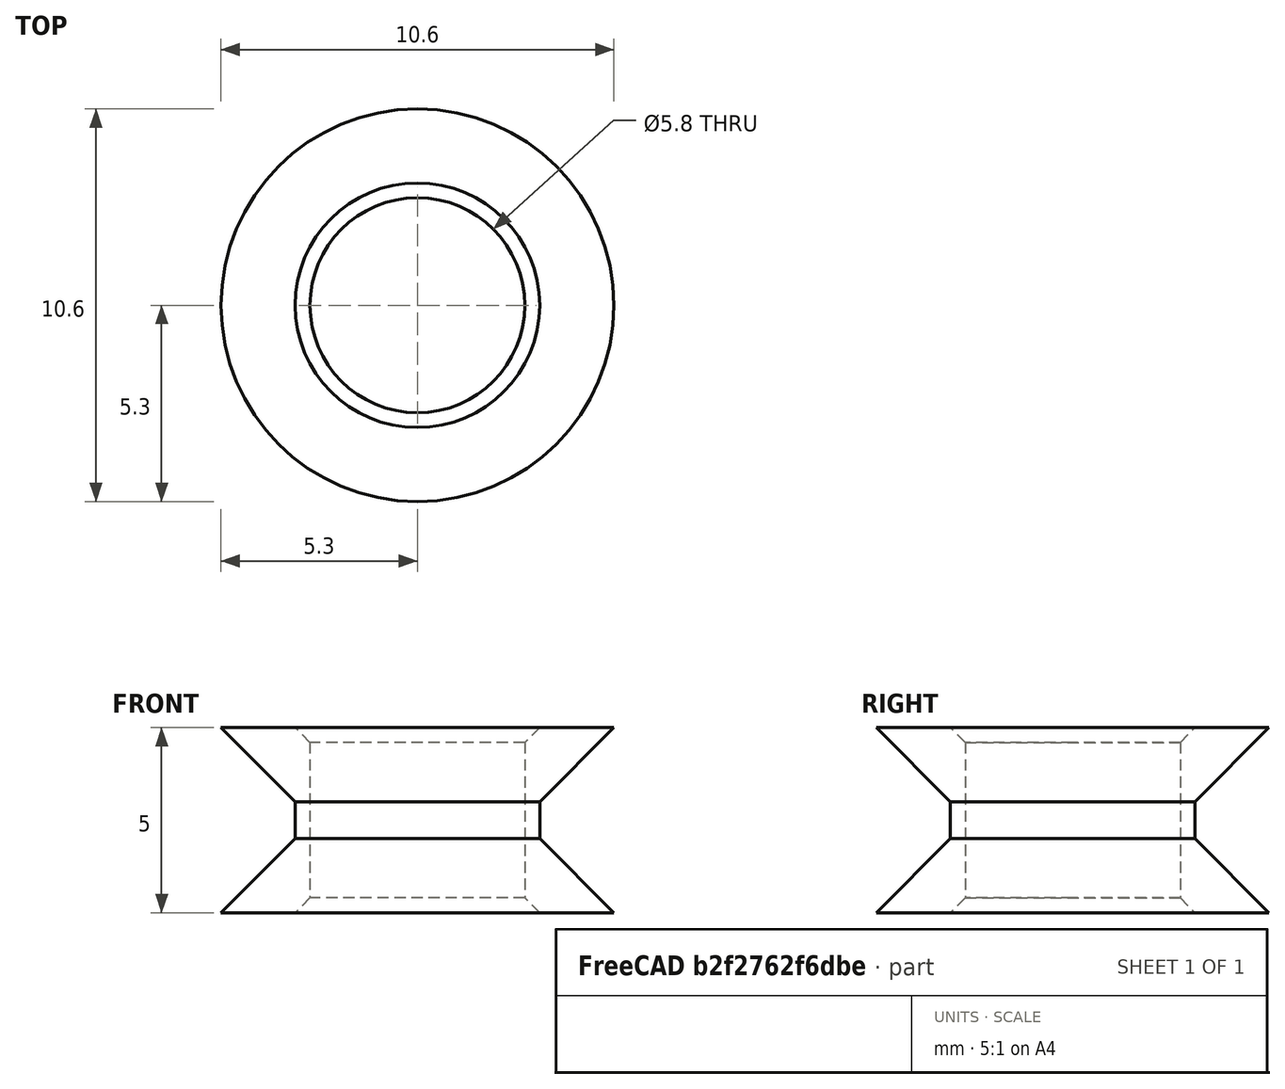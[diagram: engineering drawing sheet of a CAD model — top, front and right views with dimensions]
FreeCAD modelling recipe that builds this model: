
FCSTD DOCUMENT  (FreeCAD 0.18R4 (GitTag))
Label: Ring
License: All rights reserved
LicenseURL: http://en.wikipedia.org/wiki/All_rights_reserved
objects: Sketcher::SketchObject×1, PartDesign::Revolution×1, PartDesign::Chamfer×1, PartDesign::Body×1, Mesh::Feature×1
note: 5 computed .brp shape members not serialized (recipe doc carries the construction recipe); baked Part::Feature solids carry a one-line shape summary decoded from their .brp

FEATURE [Sketcher::SketchObject] Sketch
  MapMode = 5
  Placement = pos=(0,0,0) rot=(1,0,0;1.5708rad)
  Support = -> [XZ_Plane001]
  sketch-geometry (6):
    g0: LineSegment StartX=2.9 StartY=-2.5 StartZ=0 EndX=5.3 EndY=-2.5 EndZ=0
    g1: LineSegment StartX=5.3 StartY=-2.5 StartZ=0 EndX=3.3 EndY=-0.5 EndZ=0
    g2: LineSegment StartX=3.3 StartY=-0.5 StartZ=0 EndX=3.3 EndY=0.5 EndZ=0
    g3: LineSegment StartX=3.3 StartY=0.5 StartZ=0 EndX=5.3 EndY=2.5 EndZ=0
    g4: LineSegment StartX=5.3 StartY=2.5 StartZ=0 EndX=2.9 EndY=2.5 EndZ=0
    g5: LineSegment StartX=2.9 StartY=2.5 StartZ=0 EndX=2.9 EndY=-2.5 EndZ=0
  constraints (16):
    c: Horizontal(g0)
    c: Coincident(g0,g1)
    c: Coincident(g1,g2)
    c: Coincident(g2,g3)
    c: Coincident(g3,g4)
    c: Horizontal(g4)
    c: Coincident(g4,g5)
    c: Coincident(g5,g0)
    c: Vertical(g5)
    c: Symmetric(g2,g1,g-1)
    c: Symmetric(g3,g0,g-1)
    c: DistanceY(g5,g5) = 5
    c: DistanceY(g2,g4) = 2
    c: DistanceX(g2,g3) = 2
    c: DistanceX(g-1,g0) = 2.9
    c: DistanceX(g0,g1) = 0.4
FEATURE [PartDesign::Revolution] Revolution
  Angle = 360
  Axis = (0,2e-16,1)
  Base = (0,0,0)
  Placement = pos=(0,0,0) rot=(1,0,0;1.5708rad)
  Profile = -> Sketch
  ReferenceAxis = -> Sketch [V_Axis]
  Refine = true
  Reversed = true
FEATURE [PartDesign::Chamfer] Chamfer
  Base = -> Revolution [Face6]
  BaseFeature = -> Revolution
  Placement = pos=(0,0,0) rot=(1,0,0;1.5708rad)
  Size = 0.4
FEATURE [PartDesign::Body] Body001  label="Body"
  Group = -> [Sketch,Revolution,Chamfer]
  Origin = -> Origin001
  Tip = -> Chamfer
FEATURE [Mesh::Feature] Mesh  label="Chamfer (Meshed)"
